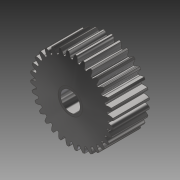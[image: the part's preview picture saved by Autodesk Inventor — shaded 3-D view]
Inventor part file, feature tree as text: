
AUTODESK INVENTOR PART (.ipt)
format: ipt  version: 2014 SP1 (Build 180222100, 222)  size: 672,768 bytes
history: native  units: in
note: dims shown in document units (in); Inventor stores cm internally (conversion verified against a paired STEP export)
features: mirror x1, other x1, imported_body x1
ambient origin geometry x8: Origin, YZ Plane, XZ Plane, XY Plane, X Axis, Y Axis, Z Axis, Center Point
bodies: Body1 (feature_tree)
feature tree (3):
  mirror  "Mirror1"
  other  "217-2625-005 Rev1_Planet_Revolving_Follower01.ipt1"
  imported_body  "Base1"
